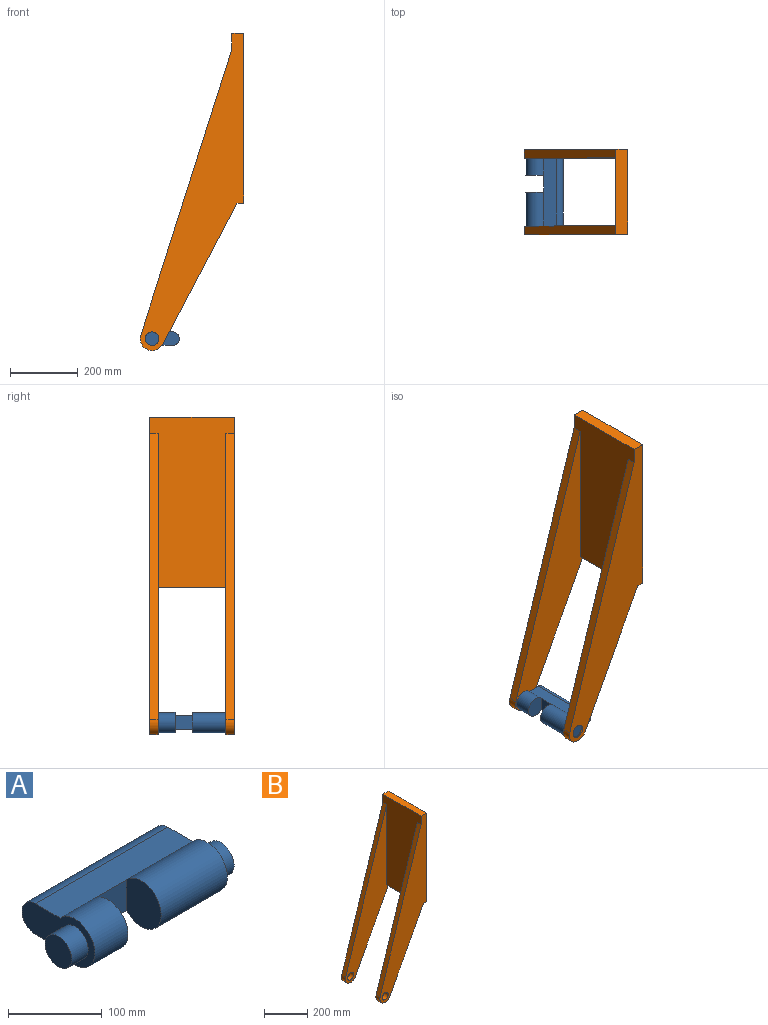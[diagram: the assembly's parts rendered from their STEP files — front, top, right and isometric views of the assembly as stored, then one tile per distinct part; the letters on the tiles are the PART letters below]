
ASSEMBLY  parts=2 mates=1
PART A: 14 faces, bbox 245x110x60 mm
  f0: cylinder r=30mm len=60mm, axis (-1,0,0), area 7235.6mm2, adj f1,f3,f6,f13
  f1: plane 200x37.64mm, normal (0,0,-1), area 7527.9mm2, adj f0,f2,f4,f5,f6,f12
  f2: cylinder r=20mm len=200mm, axis (-1,0,0), area 12566.4mm2, adj f1,f3,f5,f6
  f3: plane 200x37.64mm, normal (0,0,1), area 7527.9mm2, adj f0,f2,f4,f5,f6,f12
  f4: cylinder r=30mm len=100mm, axis (-1,0,0), area 14471.2mm2, adj f1,f3,f5,f11
  f5: plane 110x60mm, normal (1,0,0), area 3495.1mm2, adj f1,f2,f3,f4,f7
  f6: plane 110x60mm, normal (-1,0,0), area 3495.1mm2, adj f0,f1,f2,f3,f9
  f7: cylinder r=20mm len=40mm, axis (-1,0,0), area 2513.3mm2, adj f5,f8
  f8: plane 40x40mm, normal (1,0,0), area 1256.6mm2, adj f7
  f9: cylinder r=20mm len=40mm, axis (1,0,0), area 3141.6mm2, adj f6,f10
  f10: plane 40x40mm, normal (-1,0,0), area 1256.6mm2, adj f9
  f11: plane 60x52.36mm, normal (-1,0,0), area 2617.9mm2, adj f4,f12
  f12: plane 50x40mm, normal (0,-1,0), area 2000mm2, adj f1,f3,f11,f13
  f13: plane 60x52.36mm, normal (1,0,0), area 2617.9mm2, adj f0,f12
PART B: 16 faces, bbox 305x250x935 mm
  f0: plane 250x35mm, normal (0,0,-1), area 8000mm2, adj f1,f4,f6,f7,f8,f10,f12,f15
  f1: plane 887.92x285mm, normal (0,1,0), area 80479.8mm2, adj f0,f2,f3,f4,f5,f7
  f2: plane 842.29x268.35mm, normal (-0.95,0,0.3), area 22100.2mm2, adj f1,f3,f6,f7
  f3: cylinder r=35mm len=65.97mm, axis (0,1,0), area 2595mm2, adj f1,f2,f4,f6
  f4: plane 416.3x219.03mm, normal (0.88,0,-0.47), area 11760mm2, adj f0,f1,f3,f6
  f5: cylinder r=20mm len=40mm, axis (0,1,0), area 3141.6mm2, adj f1,f6
  f6: plane 935x305mm, normal (0,-1,0), area 97979.8mm2, adj f0,f2,f3,f4,f5,f7,f8,f9
  f7: plane 500x250mm, normal (-1,0,0), area 102354.1mm2, adj f0,f1,f2,f6,f9,f10,f11,f15
  f8: plane 500x250mm, normal (1,0,0), area 125000mm2, adj f0,f6,f9,f10
  f9: plane 250x35mm, normal (0,0,1), area 8750mm2, adj f6,f7,f8,f10
  f10: plane 935x305mm, normal (0,1,0), area 97979.8mm2, adj f0,f7,f8,f9,f11,f12,f13,f14
  f11: plane 842.29x268.35mm, normal (-0.95,0,0.3), area 22100.2mm2, adj f7,f10,f13,f15
  f12: plane 416.3x219.03mm, normal (0.88,0,-0.47), area 11760mm2, adj f0,f10,f13,f15
  f13: cylinder r=35mm len=65.97mm, axis (0,1,0), area 2595mm2, adj f10,f11,f12,f15
  f14: cylinder r=20mm len=40mm, axis (0,1,0), area 3141.6mm2, adj f10,f15
  f15: plane 887.92x285mm, normal (0,-1,0), area 80479.8mm2, adj f0,f7,f11,f12,f13,f14
PLACE A rot(axis=(0,0,-1),90deg) t=(-492.55,-11.34,-274.7)mm
PLACE B t=(-242.55,-211.34,51.45)mm
MATE fastened A.f0 <-> B.f3  axis (0,1,0) through (-492.55,-11.34,-274.7)mm
